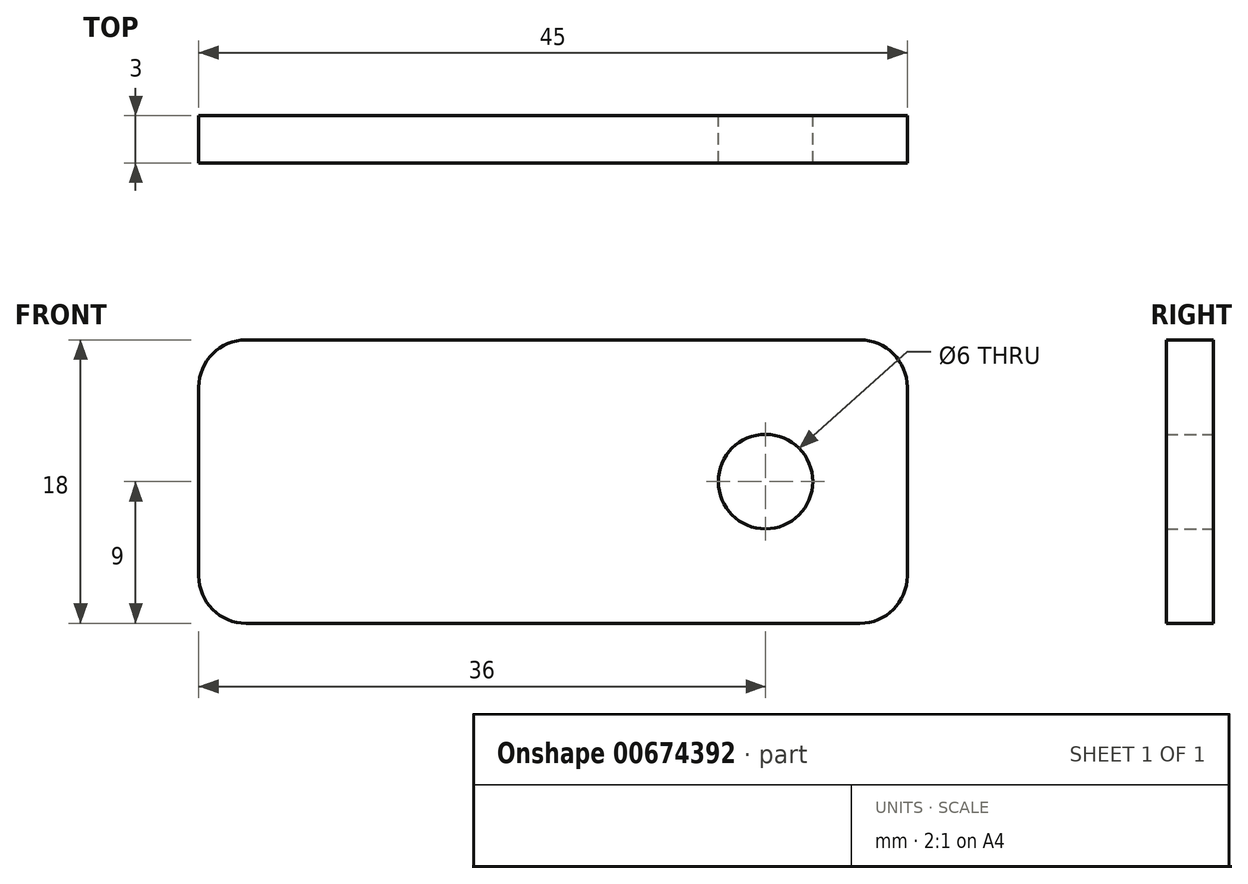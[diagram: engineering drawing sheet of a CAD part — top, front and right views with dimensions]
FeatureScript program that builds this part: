
annotation { "Feature Type Name" : "Feature", "Feature Type Description" : "" }
export const myFeature = defineFeature(function(context is Context, id is Id, definition is map)
    precondition{}
    {
        {
            var Q0;
            Q0=qCreatedBy(makeId("Front.planeOp"),FACE);
            var sketch = newSketch(context, id + "F0", { "sketchPlane" : qUnion([Q0])});
            skLineSegment(sketch, "E0.bottom", {"start": v(19.5, -9) * mm, "end": v(-19.5, -9) * mm});
            skLineSegment(sketch, "E0.top", {"start": v(19.5, 9) * mm, "end": v(-19.5, 9) * mm});
            skLineSegment(sketch, "E0.left", {"start": v(22.5, -6) * mm, "end": v(22.5, 6) * mm});
            skLineSegment(sketch, "E0.right", {"start": v(-22.5, -6) * mm, "end": v(-22.5, 6) * mm});
            skPoint(sketch, "E0.middle", {"position": v(0, 0) * mm});
            skCircle(sketch, "E1", {"center": v(13.5, 0) * mm, "radius": 3 * mm});
            skPoint(sketch, "E2.visualSharp", {"position": v(22.5, -9) * mm});
            skArc(sketch, "E2.filletArc", {"start": v(19.5, -9) * mm, "mid": v(21.62, -8.12) * mm, "end": v(22.5, -6) * mm});
            skPoint(sketch, "E3.visualSharp", {"position": v(-22.5, -9) * mm});
            skArc(sketch, "E3.filletArc", {"start": v(-22.5, -6) * mm, "mid": v(-21.62, -8.12) * mm, "end": v(-19.5, -9) * mm});
            skPoint(sketch, "E4.visualSharp", {"position": v(22.5, 9) * mm});
            skArc(sketch, "E4.filletArc", {"start": v(22.5, 6) * mm, "mid": v(21.62, 8.12) * mm, "end": v(19.5, 9) * mm});
            skPoint(sketch, "E5.visualSharp", {"position": v(-22.5, 9) * mm});
            skArc(sketch, "E5.filletArc", {"start": v(-19.5, 9) * mm, "mid": v(-21.62, 8.12) * mm, "end": v(-22.5, 6) * mm});
            skSolve(sketch);
        }
        {
            var Q0;
            Q0=makeQuery(id+"F0.imprint","IMPRINT",FACE,{"disambiguationData":[TD([[makeQuery(id+"F0.imprint","IMPRINT",EDGE,{"derivedFrom":sQuery(id+"F0.wireOp",EDGE,"E0.bottom")}),-1.0]])]});
            extrude(context, id + "F1", {"entities" : qUnion([Q0]), "depth" : 3 * mm, "offsetDistance" : 25 * mm});
        }
    });
